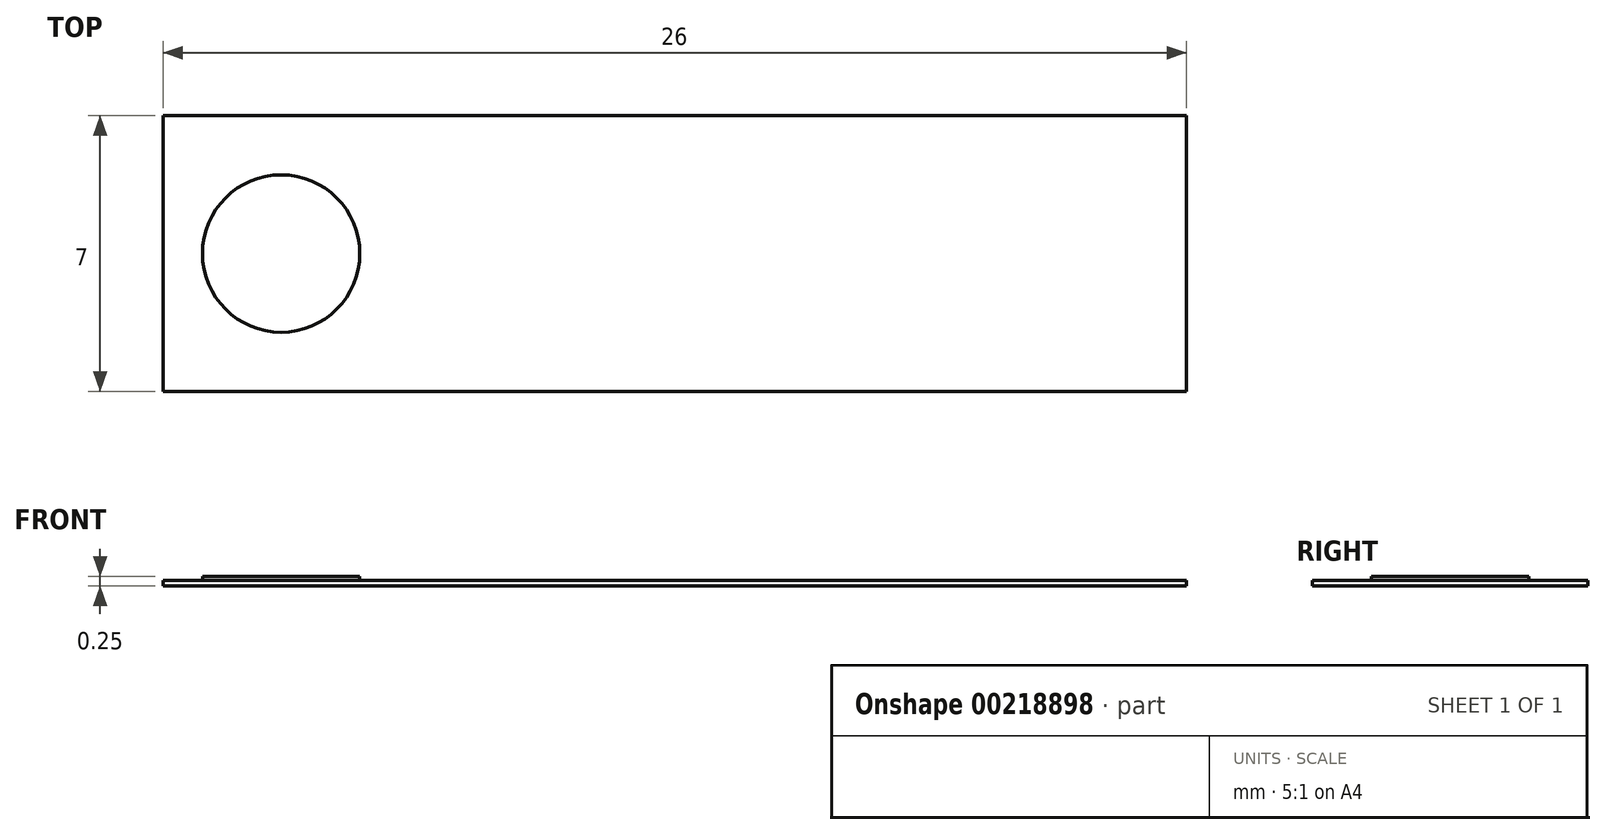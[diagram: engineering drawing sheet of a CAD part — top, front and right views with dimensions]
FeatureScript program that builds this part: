
annotation { "Feature Type Name" : "Feature", "Feature Type Description" : "" }
export const myFeature = defineFeature(function(context is Context, id is Id, definition is map)
    precondition{}
    {
        {
            var Q0;
            Q0=qCreatedBy(makeId("Top.planeOp"),FACE);
            var sketch = newSketch(context, id + "F0", { "sketchPlane" : qUnion([Q0])});
            skLineSegment(sketch, "E0.bottom", {"start": v(-13, 3.5) * mm, "end": v(13, 3.5) * mm});
            skLineSegment(sketch, "E0.top", {"start": v(-13, -3.5) * mm, "end": v(13, -3.5) * mm});
            skLineSegment(sketch, "E0.left", {"start": v(-13, 3.5) * mm, "end": v(-13, -3.5) * mm});
            skLineSegment(sketch, "E0.right", {"start": v(13, 3.5) * mm, "end": v(13, -3.5) * mm});
            skPoint(sketch, "E0.middle", {"position": v(0, 0) * mm});
            skSolve(sketch);
        }
        {
            var Q0;
            Q0=qCreatedBy(makeId("Top.planeOp"),FACE);
            var sketch = newSketch(context, id + "F1", { "sketchPlane" : qUnion([Q0])});
            skCircle(sketch, "E1", {"center": v(-10, 0) * mm, "radius": 2 * mm});
            skPoint(sketch, "E2", {"position": v(10, 0) * mm});
            skSolve(sketch);
        }
        {
            var Q0;
            Q0=makeQuery(id+"F0.imprint","IMPRINT",FACE,{"disambiguationData":[TD([[makeQuery(id+"F0.imprint","IMPRINT",EDGE,{"derivedFrom":sQuery(id+"F0.wireOp",EDGE,"E0.bottom")}),-1.0]])]});
            extrude(context, id + "F2", {"entities" : qUnion([Q0]), "oppositeDirection" : true, "depth" : .15 * mm});
        }
        {
            var Q0;
            Q0=makeQuery(id+"F1.imprint","IMPRINT",FACE,{"disambiguationData":[TD([[makeQuery(id+"F1.imprint","IMPRINT",EDGE,{"derivedFrom":sQuery(id+"F1.wireOp",EDGE,"E1")}),1.0]])]});
            extrude(context, id + "F3", {"entities" : qUnion([Q0]), "operationType" : NewBodyOperationType.ADD, "depth" : .1 * mm});
        }
    });
